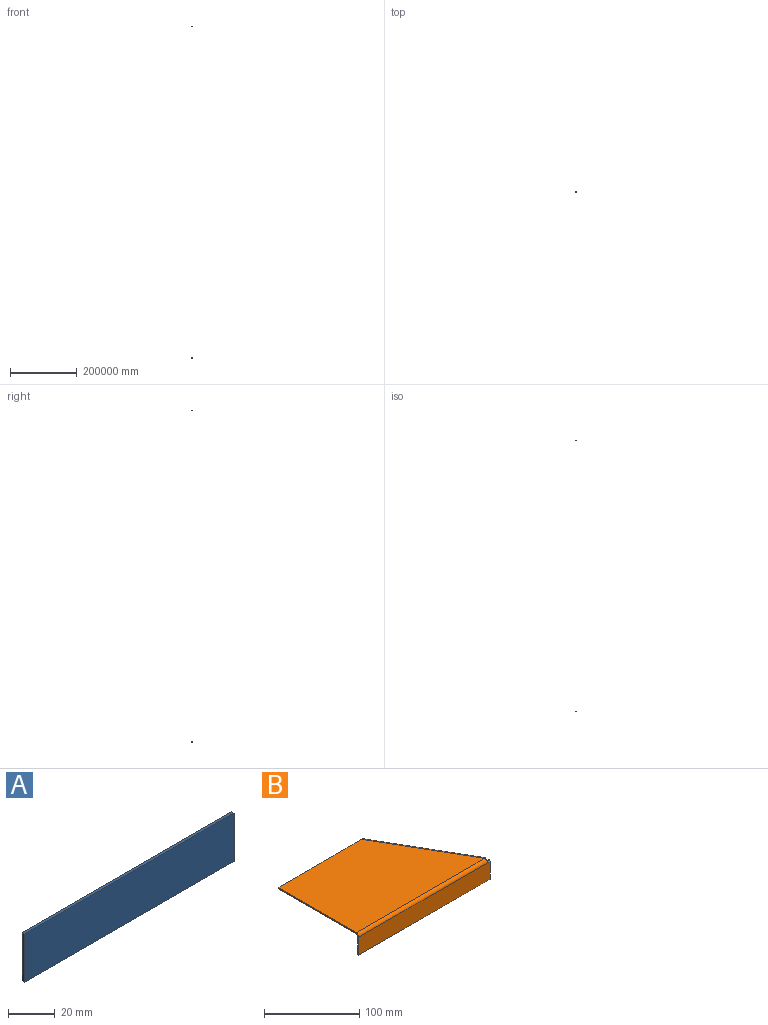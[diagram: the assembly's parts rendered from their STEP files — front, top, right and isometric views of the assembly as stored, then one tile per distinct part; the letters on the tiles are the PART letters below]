
ASSEMBLY  parts=2 mates=2
PART A: 6 faces, bbox 127x1.6x25.4 mm
  f0: plane 25.37x1.59mm, normal (-1,0,0), area 40.3mm2, adj f1,f3,f4,f5
  f1: plane 126.98x1.59mm, normal (0,0,1), area 201.6mm2, adj f0,f2,f4,f5
  f2: plane 25.37x1.59mm, normal (1,0,0), area 40.3mm2, adj f1,f3,f4,f5
  f3: plane 126.98x1.59mm, normal (0,0,-1), area 201.6mm2, adj f0,f2,f4,f5
  f4: plane 126.98x25.37mm, normal (0,1,0), area 3222.1mm2, adj f0,f1,f2,f3
  f5: plane 126.98x25.37mm, normal (0,-1,0), area 3222.1mm2, adj f0,f1,f2,f3
PART B: 24 faces, bbox 196.7x121.8x27 mm
  f0: plane 3.93x1.59mm, normal (0,0,1), area 6.2mm2, adj f3,f4,f5,f20
  f1: plane 23.11x1.59mm, normal (-1,0,0), area 36.7mm2, adj f2,f4,f5,f21
  f2: plane 195.29x1.59mm, normal (0,0,-1), area 310mm2, adj f1,f3,f4,f5
  f3: plane 23.11x1.59mm, normal (1,0,0), area 36.7mm2, adj f0,f2,f4,f5
  f4: plane 195.29x23.11mm, normal (0,-1,0), area 4514mm2, adj f0,f1,f2,f3,f22
  f5: plane 195.29x23.11mm, normal (0,1,0), area 4514mm2, adj f0,f1,f2,f3,f23
  f6: plane 116.03x1.59mm, normal (-1,0,0), area 184.2mm2, adj f7,f8,f9,f21
  f7: plane 124.38x1.59mm, normal (0,1,0), area 197.4mm2, adj f6,f8,f9,f17
  f8: plane 191.36x116.03mm, normal (0,0,1), area 18317.3mm2, adj f6,f7,f18,f22
  f9: plane 191.36x116.03mm, normal (0,0,-1), area 18317.3mm2, adj f6,f7,f19,f23
  f10: plane 4.2x3.34mm, normal (0,0,1), area 6.2mm2, adj f11,f14,f15,f16
  f11: plane 23.11x1.38mm, normal (0.5,-0.87,0), area 36.7mm2, adj f10,f12,f14,f15
  f12: plane 119.09x69.68mm, normal (0,0,-1), area 216.9mm2, adj f11,f13,f14,f15
  f13: plane 23.11x1.38mm, normal (-0.5,0.87,0), area 36.7mm2, adj f12,f14,f15,f17
  f14: plane 118.3x68.3mm, normal (0.87,0.5,0), area 3157.4mm2, adj f10,f11,f12,f13,f18
  f15: plane 118.3x68.3mm, normal (-0.87,-0.5,0), area 3157.4mm2, adj f10,f11,f12,f13,f19
  f16: plane 3.87x3.35mm, normal (0.5,-0.87,0), area 7.7mm2, adj f10,f18,f19,f20
  f17: bspline ~4.02x3.87mm, area 8.1mm2, adj f7,f13,f18,f19
  f18: cylinder r=3.87mm len=117.97mm, axis (0.5,-0.87,0), area 809.4mm2, adj f8,f14,f16,f17
  f19: cylinder r=2.29mm len=117.17mm, axis (0.5,-0.87,0), area 477.7mm2, adj f9,f15,f16,f17
  f20: plane 3.87x3.87mm, normal (1,0,0), area 7.7mm2, adj f0,f16,f22,f23
  f21: plane 3.87x3.87mm, normal (-1,0,0), area 7.7mm2, adj f1,f6,f22,f23
  f22: cylinder r=3.87mm len=191.36mm, axis (1,0,0), area 1164.4mm2, adj f4,f8,f20,f21
  f23: cylinder r=2.29mm len=191.36mm, axis (1,0,0), area 687.2mm2, adj f5,f9,f20,f21
PLACE A rot(axis=(-0.13,0.7,-0.7),165.6deg) t=(-120.53,46.61,-995366.82)mm
PLACE B t=(-11.72,0,0)mm fixed
MATE parallel A.f4 <-> B.f8  axis (0,0,-1) through (-56.6,56.94,-995486.75)mm
MATE parallel B.f8 <-> A.f4  axis (0,0,1) through (-58.6,56.2,26.99)mm
